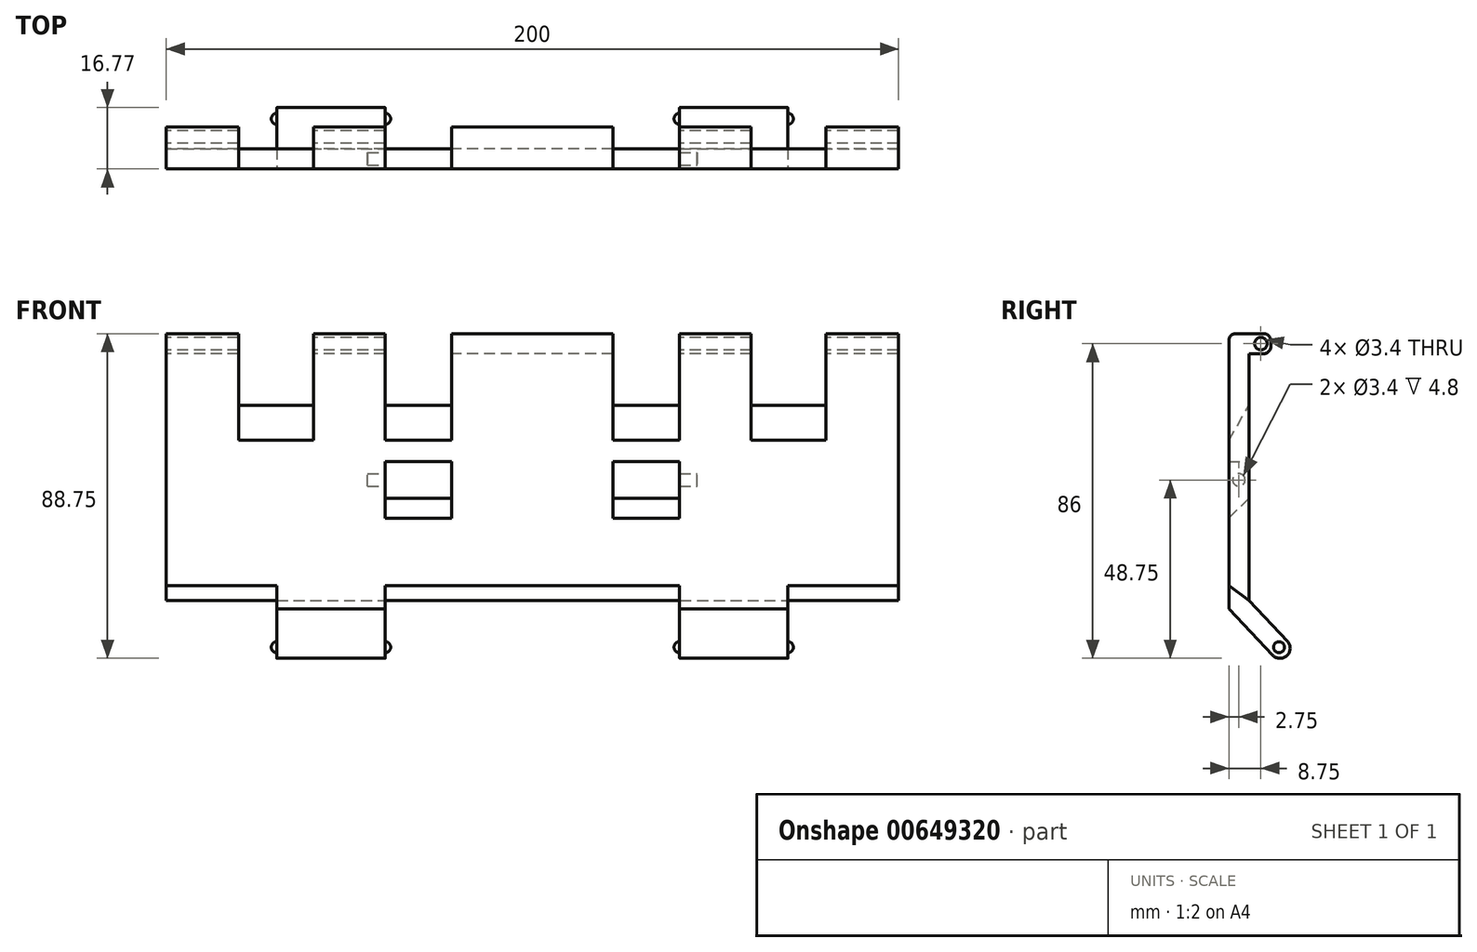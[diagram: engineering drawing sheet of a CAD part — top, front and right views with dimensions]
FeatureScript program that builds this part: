
annotation { "Feature Type Name" : "Feature", "Feature Type Description" : "" }
export const myFeature = defineFeature(function(context is Context, id is Id, definition is map)
    precondition{}
    {
        {
            var Q0;
            Q0=qCreatedBy(makeId("Right.planeOp"),FACE);
            var sketch = newSketch(context, id + "F0", { "sketchPlane" : qUnion([Q0])});
            skLineSegment(sketch, "E0", {"start": v(0.26, 88) * mm, "end": v(0.26, 2) * mm, "construction": true});
            skLineSegment(sketch, "E1", {"start": v(-1.74, 0) * mm, "end": v(-15.13, 0) * mm, "construction": true});
            skLineSegment(sketch, "E2", {"start": v(-5.13, 43.95) * mm, "end": v(-5.13, 88) * mm, "construction": true});
            skLineSegment(sketch, "E3", {"start": v(-3.13, 90) * mm, "end": v(-1.74, 90) * mm, "construction": true});
            skPoint(sketch, "E4.visualSharp", {"position": v(1.01, 9.5) * mm});
            skPoint(sketch, "E5.visualSharp", {"position": v(-10.99, 10.5) * mm});
            skPoint(sketch, "E6.visualSharp", {"position": v(-10.99, 3.5) * mm});
            skArc(sketch, "E6.filletArc", {"start": v(-17.13, 2) * mm, "mid": v(-16.54, 0.59) * mm, "end": v(-15.13, 0) * mm, "construction": true});
            skPoint(sketch, "E7.visualSharp", {"position": v(7.01, 3.5) * mm});
            skArc(sketch, "E7.filletArc", {"start": v(-1.74, 0) * mm, "mid": v(-0.33, 0.59) * mm, "end": v(0.26, 2) * mm, "construction": true});
            skPoint(sketch, "E8.visualSharp", {"position": v(6.51, 93.5) * mm});
            skArc(sketch, "E8.filletArc", {"start": v(0.26, 88) * mm, "mid": v(-0.33, 89.41) * mm, "end": v(-1.74, 90) * mm, "construction": true});
            skPoint(sketch, "E9.visualSharp", {"position": v(1.01, 93.5) * mm});
            skArc(sketch, "E9.filletArc", {"start": v(-3.13, 90) * mm, "mid": v(-4.54, 89.41) * mm, "end": v(-5.13, 88) * mm, "construction": true});
            skLineSegment(sketch, "E10", {"start": v(-9.46, 6.36) * mm, "end": v(-16.04, 6.9) * mm, "construction": true});
            skLineSegment(sketch, "E11", {"start": v(-17.13, 2) * mm, "end": v(-17.13, 5.91) * mm, "construction": true});
            skArc(sketch, "E12.filletArc", {"start": v(-16.04, 6.9) * mm, "mid": v(-16.8, 6.65) * mm, "end": v(-17.13, 5.91) * mm, "construction": true});
            skLineSegment(sketch, "E13", {"start": v(-5.13, 43.95) * mm, "end": v(-5.13, 9.26) * mm, "construction": true});
            skLineSegment(sketch, "E14", {"start": v(-9.46, 6.36) * mm, "end": v(-8.38, 6.27) * mm, "construction": true});
            skArc(sketch, "E15.filletArc", {"start": v(-8.38, 6.27) * mm, "mid": v(-6.1, 7.05) * mm, "end": v(-5.13, 9.26) * mm, "construction": true});
            skCircle(sketch, "E16", {"center": v(-4, 4) * mm, "radius": 2.75 * mm});
            skLineSegment(sketch, "E17", {"start": v(-12.5, 80) * mm, "end": v(-12.5, 17) * mm});
            skLineSegment(sketch, "E18", {"start": v(-12.5, 17) * mm, "end": v(-2, 5.89) * mm});
            skLineSegment(sketch, "E19", {"start": v(-18, 14.81) * mm, "end": v(-6, 2.11) * mm});
            skLineSegment(sketch, "E20", {"start": v(-18, 79) * mm, "end": v(-18, 14.81) * mm});
            skLineSegment(sketch, "E21", {"start": v(-2, 5.89) * mm, "end": v(-6, 2.11) * mm});
            skLineSegment(sketch, "E22", {"start": v(-18, 79) * mm, "end": v(-18, 88) * mm});
            skLineSegment(sketch, "E23", {"start": v(-16, 90) * mm, "end": v(-8.5, 90) * mm});
            skLineSegment(sketch, "E24", {"start": v(-6.5, 88) * mm, "end": v(-6.5, 86.5) * mm});
            skLineSegment(sketch, "E25", {"start": v(-8.5, 84.5) * mm, "end": v(-12.5, 84.5) * mm});
            skLineSegment(sketch, "E26", {"start": v(-12.5, 84.5) * mm, "end": v(-12.5, 80) * mm});
            skLineSegment(sketch, "E27", {"start": v(-12.5, 84.5) * mm, "end": v(-18, 79) * mm});
            skPoint(sketch, "E28.visualSharp", {"position": v(-6.5, 90) * mm});
            skArc(sketch, "E28.filletArc", {"start": v(-6.5, 88) * mm, "mid": v(-7.09, 89.41) * mm, "end": v(-8.5, 90) * mm});
            skPoint(sketch, "E29.visualSharp", {"position": v(-6.5, 84.5) * mm});
            skArc(sketch, "E29.filletArc", {"start": v(-8.5, 84.5) * mm, "mid": v(-7.09, 85.09) * mm, "end": v(-6.5, 86.5) * mm});
            skPoint(sketch, "E30.visualSharp", {"position": v(-18, 90) * mm});
            skArc(sketch, "E30.filletArc", {"start": v(-16, 90) * mm, "mid": v(-17.41, 89.41) * mm, "end": v(-18, 88) * mm});
            skSolve(sketch);
        }
        {
            var Q0;
            Q0 = qSketchRegion(id + "FafqnAbmj27rbiK_0", true);
            var Q1;
            Q1 = qSketchRegion(id + "F0", true);
            extrude(context, id + "F1", {"entities" : qUnion([Q0, Q1]), "depth" : 100 * mm, "offsetDistance" : 25 * mm, "hasSecondDirection" : true, "secondDirectionOppositeDirection" : true, "secondDirectionDepth" : 100 * mm});
        }
        {
            var Q0;
            Q0=qCreatedBy(makeId("Right.planeOp"),FACE);
            var sketch = newSketch(context, id + "F2", { "sketchPlane" : qUnion([Q0])});
            skCircle(sketch, "E31", {"center": v(-9.25, 87.25) * mm, "radius": 1.7 * mm});
            skSolve(sketch);
        }
        {
            var Q0;
            Q0=qCreatedBy(makeId("Right.planeOp"),FACE);
            var sketch = newSketch(context, id + "F3", { "sketchPlane" : qUnion([Q0])});
            skLineSegment(sketch, "E32", {"start": v(-12, 71.26) * mm, "end": v(-18.5, 60) * mm});
            skLineSegment(sketch, "E33", {"start": v(-18.5, 60) * mm, "end": v(-18.5, 87.76) * mm});
            skLineSegment(sketch, "E34", {"start": v(-18.5, 87.76) * mm, "end": v(-18.5, 90) * mm});
            skLineSegment(sketch, "E35", {"start": v(-18.5, 90) * mm, "end": v(-5.5, 90) * mm});
            skLineSegment(sketch, "E36", {"start": v(-5.5, 90) * mm, "end": v(-5.5, 84.5) * mm});
            skLineSegment(sketch, "E37", {"start": v(-5.5, 84.5) * mm, "end": v(-12, 84.5) * mm});
            skLineSegment(sketch, "E38", {"start": v(-12, 84.5) * mm, "end": v(-12, 71.26) * mm});
            skSolve(sketch);
        }
        {
            var Q0;
            Q0 = qSketchRegion(id + "F3", true);
            extrude(context, id + "F4", {"entities" : qUnion([Q0]), "operationType" : NewBodyOperationType.REMOVE, "oppositeDirection" : true, "depth" : 80.2 * mm, "offsetDistance" : 25 * mm, "hasSecondDirection" : true, "secondDirectionOppositeDirection" : false, "secondDirectionDepth" : 80.2 * mm});
        }
        {
            var Q0;
            Q0 = qSketchRegion(id + "F0", true);
            extrude(context, id + "F5", {"entities" : qUnion([Q0]), "operationType" : NewBodyOperationType.ADD, "depth" : 59.8 * mm, "offsetDistance" : 25 * mm, "hasSecondDirection" : true, "secondDirectionOppositeDirection" : true, "secondDirectionDepth" : 59.8 * mm});
        }
        {
            var Q0;
            Q0=qCreatedBy(makeId("Right.planeOp"),FACE);
            var sketch = newSketch(context, id + "F6", { "sketchPlane" : qUnion([Q0])});
            skCircle(sketch, "E39", {"center": v(-15.25, 50) * mm, "radius": 1.5 * mm});
            skLineSegment(sketch, "E40", {"start": v(-18, 39.5) * mm, "end": v(-12.5, 45) * mm});
            skLineSegment(sketch, "E41", {"start": v(-12.5, 45) * mm, "end": v(-12.5, 55) * mm});
            skLineSegment(sketch, "E42", {"start": v(-12.5, 55) * mm, "end": v(-18, 55) * mm});
            skLineSegment(sketch, "E43", {"start": v(-18, 55) * mm, "end": v(-18, 39.5) * mm});
            skLineSegment(sketch, "E44", {"start": v(-18.48, 90) * mm, "end": v(-6.06, 90) * mm});
            skLineSegment(sketch, "E45", {"start": v(-6.06, 90) * mm, "end": v(-6.06, 84.5) * mm});
            skLineSegment(sketch, "E46", {"start": v(-6.06, 84.5) * mm, "end": v(-12.5, 84.5) * mm});
            skLineSegment(sketch, "E47", {"start": v(-12.5, 84.5) * mm, "end": v(-12.5, 79.5) * mm});
            skLineSegment(sketch, "E48", {"start": v(-12.5, 79.5) * mm, "end": v(-18.48, 73.52) * mm});
            skLineSegment(sketch, "E49", {"start": v(-18.48, 73.52) * mm, "end": v(-18.48, 90) * mm});
            skSolve(sketch);
        }
        {
            var Q0;
            Q0 = qSketchRegion(id + "F6", true);
            extrude(context, id + "F7", {"entities" : qUnion([Q0]), "operationType" : NewBodyOperationType.REMOVE, "oppositeDirection" : true, "depth" : 40.2 * mm, "offsetDistance" : 25 * mm, "hasSecondDirection" : true, "secondDirectionOppositeDirection" : false, "secondDirectionDepth" : 40.2 * mm});
        }
        {
            var Q0;
            Q0=qCreatedBy(makeId("Right.planeOp"),FACE);
            var sketch = newSketch(context, id + "F8", { "sketchPlane" : qUnion([Q0])});
            skCircle(sketch, "E50", {"center": v(-15.25, 50) * mm, "radius": 1.7 * mm});
            skSolve(sketch);
        }
        {
            var Q0;
            Q0 = qSketchRegion(id + "F0", true);
            extrude(context, id + "F9", {"entities" : qUnion([Q0]), "operationType" : NewBodyOperationType.ADD, "depth" : 19.8 * mm, "offsetDistance" : 25 * mm, "hasSecondDirection" : true, "secondDirectionOppositeDirection" : true, "secondDirectionDepth" : 19.8 * mm});
        }
        {
            var Q0;
            Q0 = qSketchRegion(id + "F2", true);
            extrude(context, id + "F10", {"entities" : qUnion([Q0]), "operationType" : NewBodyOperationType.REMOVE, "endBound" : BoundingType.THROUGH_ALL, "depth" : 25 * mm, "offsetDistance" : 25 * mm, "hasSecondDirection" : true, "secondDirectionBound" : SecondDirectionBoundingType.THROUGH_ALL, "secondDirectionOppositeDirection" : true, "secondDirectionDepth" : 25 * mm});
        }
        {
            var Q0;
            Q0 = qSketchRegion(id + "F8", true);
            extrude(context, id + "F11", {"entities" : qUnion([Q0]), "operationType" : NewBodyOperationType.REMOVE, "oppositeDirection" : true, "depth" : 45 * mm, "offsetDistance" : 25 * mm, "hasSecondDirection" : true, "secondDirectionOppositeDirection" : false, "secondDirectionDepth" : 45 * mm});
        }
        {
            var Q0;
            Q0=qCreatedBy(makeId("Right.planeOp"),FACE);
            var sketch = newSketch(context, id + "F12", { "sketchPlane" : qUnion([Q0])});
            skLineSegment(sketch, "E51", {"start": v(-12.5, 17) * mm, "end": v(-1.98, 5.9) * mm});
            skLineSegment(sketch, "E52", {"start": v(-6, 2.1) * mm, "end": v(-18, 14.8) * mm});
            skArc(sketch, "E53", {"start": v(-6, 2.1) * mm, "mid": v(-2.1, 2) * mm, "end": v(-1.98, 5.9) * mm});
            skLineSegment(sketch, "E54", {"start": v(-12.5, 17) * mm, "end": v(-18, 21.08) * mm});
            skLineSegment(sketch, "E55", {"start": v(-18, 21.08) * mm, "end": v(-18, 14.8) * mm});
            skSolve(sketch);
        }
        {
            var Q0;
            Q0 = qSketchRegion(id + "F12", true);
            extrude(context, id + "F13", {"entities" : qUnion([Q0]), "operationType" : NewBodyOperationType.REMOVE, "depth" : 100 * mm, "offsetDistance" : 25 * mm, "hasSecondDirection" : true, "secondDirectionOppositeDirection" : true, "secondDirectionDepth" : 100 * mm});
        }
        {
            var Q0;
            Q0 = qSketchRegion(id + "F12", true);
            extrude(context, id + "F14", {"entities" : qUnion([Q0]), "operationType" : NewBodyOperationType.ADD, "depth" : 69.8 * mm, "offsetDistance" : 25 * mm, "hasSecondDirection" : true, "secondDirectionOppositeDirection" : true, "secondDirectionDepth" : 69.8 * mm});
        }
        {
            var Q0;
            Q0 = qSketchRegion(id + "F12", true);
            extrude(context, id + "F15", {"entities" : qUnion([Q0]), "operationType" : NewBodyOperationType.REMOVE, "depth" : 40.2 * mm, "offsetDistance" : 25 * mm, "hasSecondDirection" : true, "secondDirectionOppositeDirection" : true, "secondDirectionDepth" : 40.2 * mm});
        }
        {
            var Q0;
            Q0=makeQuery(id+"F14.opExtrude","CAP_FACE",FACE,{"disambiguationData":[OSD([sQuery(id+"F12.wireOp",EDGE,"XtFTnGoI-2OzL-Q1O9-jpMc-cZYnFpfTudZ5"),sQuery(id+"F12.wireOp",EDGE,"E51"),sQuery(id+"F12.wireOp",EDGE,"E52"),sQuery(id+"F12.wireOp",EDGE,"E53")])],"isStart":false});
            var sketch = newSketch(context, id + "F16", { "sketchPlane" : qUnion([Q0])});
            skCircle(sketch, "E56", {"center": v(-4.3, 4.3) * mm, "radius": 1.5 * mm});
            skSolve(sketch);
        }
        {
            var Q0;
            Q0 = qSketchRegion(id + "F16", true);
            extrude(context, id + "F17", {"entities" : qUnion([Q0]), "operationType" : NewBodyOperationType.ADD, "depth" : 1.5 * mm, "offsetDistance" : 25 * mm, "hasSecondDirection" : true, "secondDirectionOppositeDirection" : true, "secondDirectionDepth" : 31.1 * mm});
        }
        {
            var Q0;
            Q0=makeQuery(id+"F15.boolean.opBoolean","COPY",FACE,{"derivedFrom":makeQuery(id+"F15.opExtrude","CAP_FACE",FACE,{"disambiguationData":[OSD([sQuery(id+"F12.wireOp",EDGE,"XtFTnGoI-2OzL-Q1O9-jpMc-cZYnFpfTudZ5"),sQuery(id+"F12.wireOp",EDGE,"E51"),sQuery(id+"F12.wireOp",EDGE,"E52"),sQuery(id+"F12.wireOp",EDGE,"E53")])],"isStart":true})});
            var sketch = newSketch(context, id + "F18", { "sketchPlane" : qUnion([Q0])});
            skCircle(sketch, "E57", {"center": v(-4.3, 4.3) * mm, "radius": 1.5 * mm});
            skSolve(sketch);
        }
        {
            var Q0;
            Q0 = qSketchRegion(id + "F18", true);
            extrude(context, id + "F19", {"entities" : qUnion([Q0]), "operationType" : NewBodyOperationType.ADD, "depth" : 1.5 * mm, "offsetDistance" : 25 * mm, "hasSecondDirection" : true, "secondDirectionOppositeDirection" : true, "secondDirectionDepth" : 31.1 * mm});
        }
        {
            var Q0;
            Q0=makeQuery(id+"F17.opExtrude","CAP_EDGE",EDGE,{"disambiguationData":[OSD([sQuery(id+"F16.wireOp",EDGE,"E56")])],"isStart":false});
            var Q1;
            Q1=makeQuery(id+"F17.opExtrude","CAP_EDGE",EDGE,{"disambiguationData":[OSD([sQuery(id+"F16.wireOp",EDGE,"E56")])],"isStart":true});
            var Q2;
            Q2=makeQuery(id+"F19.opExtrude","CAP_EDGE",EDGE,{"disambiguationData":[OSD([sQuery(id+"F18.wireOp",EDGE,"E57")])],"isStart":false});
            var Q3;
            Q3=makeQuery(id+"F19.opExtrude","CAP_EDGE",EDGE,{"disambiguationData":[OSD([sQuery(id+"F18.wireOp",EDGE,"E57")])],"isStart":true});
            fillet(context, id + "F20", {"entities" : qUnion([Q0, Q1, Q2, Q3]), "radius" : 1.5 * mm, "tangentPropagation" : true, "allowEdgeOverflow" : false});
        }
        {
            var Q0;
            Q0 = qSketchRegion(id + "F3", true);
            extrude(context, id + "F21", {"entities" : qUnion([Q0]), "operationType" : NewBodyOperationType.REMOVE, "oppositeDirection" : true, "depth" : 40.2 * mm, "offsetDistance" : 25 * mm, "hasSecondDirection" : true, "secondDirectionOppositeDirection" : false, "secondDirectionDepth" : 40.2 * mm});
        }
        {
            var Q0;
            Q0 = qSketchRegion(id + "F0", true);
            extrude(context, id + "F22", {"entities" : qUnion([Q0]), "operationType" : NewBodyOperationType.ADD, "depth" : 22 * mm, "offsetDistance" : 25 * mm, "hasSecondDirection" : true, "secondDirectionOppositeDirection" : true, "secondDirectionDepth" : 22 * mm});
        }
        {
            var Q0;
            Q0 = qSketchRegion(id + "F12", true);
            extrude(context, id + "F23", {"entities" : qUnion([Q0]), "operationType" : NewBodyOperationType.REMOVE, "depth" : 25 * mm, "offsetDistance" : 25 * mm, "hasSecondDirection" : true, "secondDirectionOppositeDirection" : true, "secondDirectionDepth" : 25 * mm});
        }
    });
